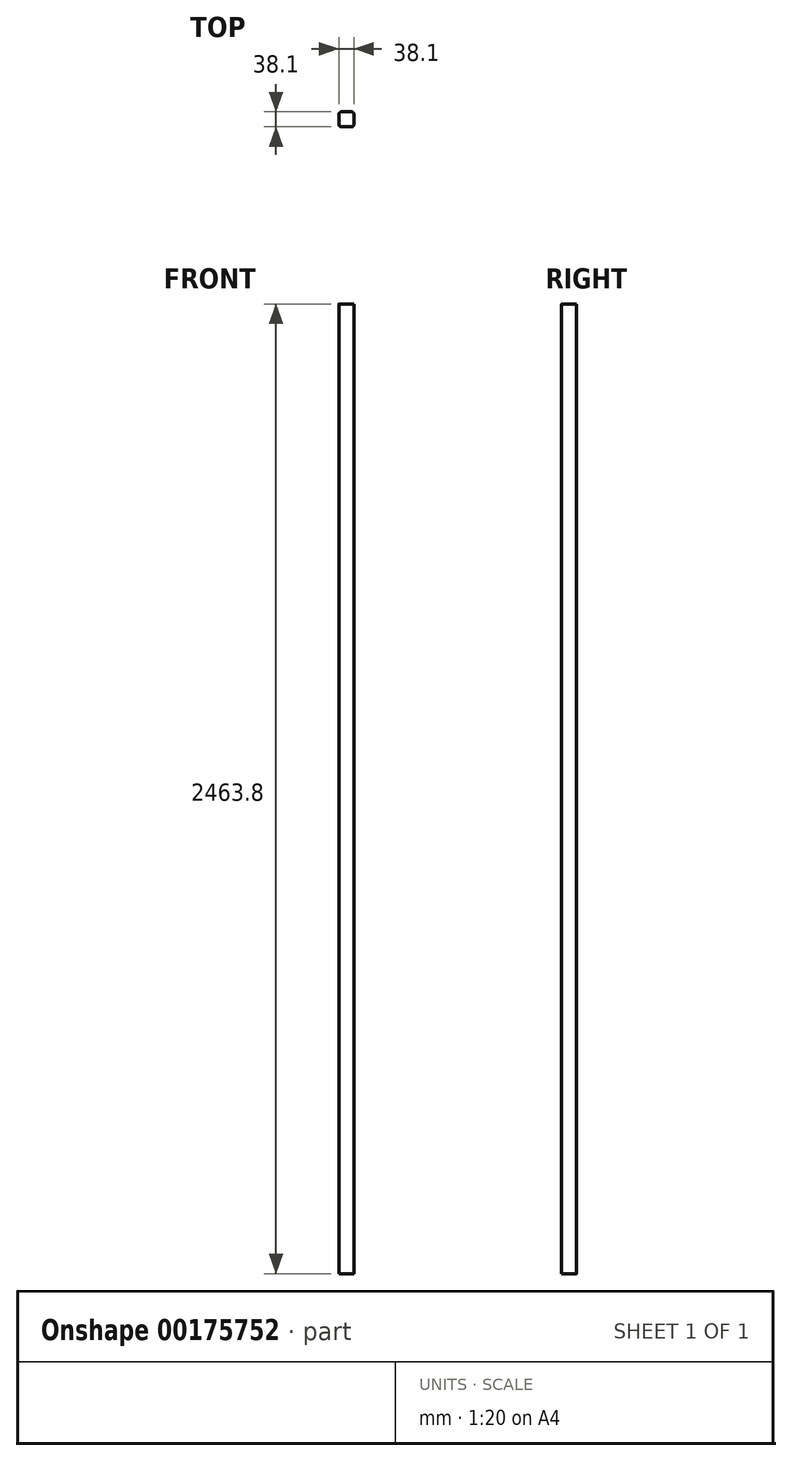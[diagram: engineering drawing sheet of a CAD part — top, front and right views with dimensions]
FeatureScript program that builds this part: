
annotation { "Feature Type Name" : "Feature", "Feature Type Description" : "" }
export const myFeature = defineFeature(function(context is Context, id is Id, definition is map)
    precondition{}
    {
        {
            var Q0;
            Q0=qCreatedBy(makeId("Top.planeOp"),FACE);
            var sketch = newSketch(context, id + "F0", { "sketchPlane" : qUnion([Q0])});
            skLineSegment(sketch, "E0.bottom", {"start": v(12.7, 19.05) * mm, "end": v(-12.7, 19.05) * mm});
            skLineSegment(sketch, "E0.top", {"start": v(12.7, -19.05) * mm, "end": v(-12.7, -19.05) * mm});
            skLineSegment(sketch, "E0.left", {"start": v(19.05, 12.7) * mm, "end": v(19.05, -12.7) * mm});
            skLineSegment(sketch, "E0.right", {"start": v(-19.05, 12.7) * mm, "end": v(-19.05, -12.7) * mm});
            skPoint(sketch, "E0.middle", {"position": v(0, 0) * mm});
            skPoint(sketch, "E1.visualSharp", {"position": v(19.05, 19.05) * mm});
            skArc(sketch, "E1.filletArc", {"start": v(19.05, 12.7) * mm, "mid": v(17.2, 17.2) * mm, "end": v(12.7, 19.05) * mm});
            skPoint(sketch, "E2.visualSharp", {"position": v(-19.05, 19.05) * mm});
            skArc(sketch, "E2.filletArc", {"start": v(-12.7, 19.05) * mm, "mid": v(-17.2, 17.2) * mm, "end": v(-19.05, 12.7) * mm});
            skPoint(sketch, "E3.visualSharp", {"position": v(-19.05, -19.05) * mm});
            skArc(sketch, "E3.filletArc", {"start": v(-19.05, -12.7) * mm, "mid": v(-17.2, -17.2) * mm, "end": v(-12.7, -19.05) * mm});
            skPoint(sketch, "E4.visualSharp", {"position": v(19.05, -19.05) * mm});
            skArc(sketch, "E4.filletArc", {"start": v(12.7, -19.05) * mm, "mid": v(17.2, -17.2) * mm, "end": v(19.05, -12.7) * mm});
            skSolve(sketch);
        }
        {
            var Q0;
            Q0=qSketchRegion(id+"F0",true);
            extrude(context, id + "F1", {"entities" : qUnion([Q0]), "depth" : 2463.8 * mm});
        }
    });
